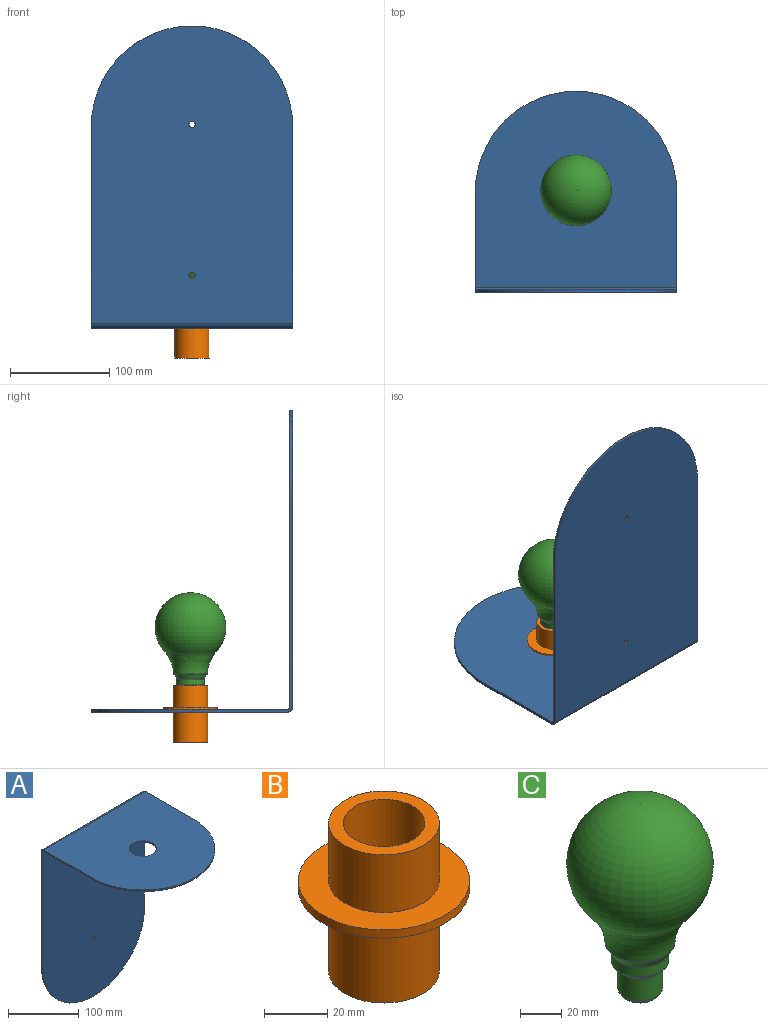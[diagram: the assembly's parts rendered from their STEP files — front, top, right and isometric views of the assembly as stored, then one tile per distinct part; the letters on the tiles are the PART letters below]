
ASSEMBLY  parts=3 mates=1
PART A: 17 faces, bbox 203.2x203.2x304.8 mm
  f0: plane 198.14x2.78mm, normal (1,0,0), area 550.4mm2, adj f4,f5,f6,f13
  f1: plane 198.14x2.78mm, normal (-1,0,0), area 550.4mm2, adj f4,f5,f6,f14
  f2: cylinder r=3.17mm len=6.35mm, axis (0,-1,0), area 55.4mm2, adj f5,f6
  f3: cylinder r=3.17mm len=6.35mm, axis (0,-1,0), area 55.4mm2, adj f5,f6
  f4: cylinder r=101.6mm len=203.2mm, axis (0,-1,0), area 886.7mm2, adj f0,f1,f5,f6
  f5: plane 299.74x203.2mm, normal (0,-1,0), area 56412.5mm2, adj f0,f1,f2,f3,f4,f16
  f6: plane 299.74x203.2mm, normal (0,1,0), area 56412.5mm2, adj f0,f1,f2,f3,f4,f15
  f7: plane 96.54x2.78mm, normal (1,0,0), area 268.2mm2, adj f8,f11,f12,f13
  f8: cylinder r=101.6mm len=203.2mm, axis (0,0,-1), area 886.7mm2, adj f7,f10,f11,f12
  f9: cylinder r=19.05mm len=38.1mm, axis (0,0,-1), area 332.5mm2, adj f11,f12
  f10: plane 96.54x2.78mm, normal (-1,0,0), area 268.2mm2, adj f8,f11,f12,f14
  f11: plane 203.2x198.14mm, normal (0,0,-1), area 34690.6mm2, adj f7,f8,f9,f10,f16
  f12: plane 203.2x198.14mm, normal (0,0,1), area 34690.6mm2, adj f7,f8,f9,f10,f15
  f13: plane 5.06x5.06mm, normal (1,0,0), area 16mm2, adj f0,f7,f15,f16
  f14: plane 5.06x5.06mm, normal (-1,0,0), area 16mm2, adj f1,f10,f15,f16
  f15: cylinder r=5.06mm len=203.2mm, axis (1,0,0), area 1616.4mm2, adj f6,f12,f13,f14
  f16: cylinder r=2.29mm len=203.2mm, axis (1,0,0), area 729.7mm2, adj f5,f11,f13,f14
PART B: 9 faces, bbox 54x54x57.2 mm
  f0: cylinder r=17.46mm len=34.93mm, axis (0,0,-1), area 3483.6mm2, adj f1,f3
  f1: plane 34.93x34.93mm, normal (0,0,-1), area 958mm2, adj f0
  f2: plane 53.98x53.98mm, normal (0,0,1), area 1330.1mm2, adj f4,f5
  f3: plane 53.98x53.98mm, normal (0,0,-1), area 1330.1mm2, adj f0,f4
  f4: cylinder r=26.99mm len=53.98mm, axis (0,0,-1), area 538.4mm2, adj f2,f3
  f5: cylinder r=17.46mm len=34.93mm, axis (0,0,-1), area 2438.5mm2, adj f2,f6
  f6: plane 34.93x34.93mm, normal (0,0,1), area 435.6mm2, adj f5,f7
  f7: cylinder r=12.9mm len=25.79mm, axis (0,0,1), area 1800.8mm2, adj f6,f8
  f8: plane 25.79x25.79mm, normal (0,0,1), area 522.4mm2, adj f7
PART C: 16 faces, bbox 71.4x71.4x112 mm
  f0: torus R=54.7mm, axis (0,0,1), area 2760.8mm2, adj f9,f15
  f1: cone r=17mm half-angle=31deg, axis (0,0,1), area 516.6mm2, adj f9,f10
  f2: cylinder r=14mm len=28mm, axis (0,0,1), area 467mm2, adj f10,f11
  f3: cone r=14mm half-angle=45deg, axis (0,0,1), area 268.2mm2, adj f11,f12
  f4: cylinder r=11mm len=22mm, axis (0,0,1), area 869.9mm2, adj f5,f12
  f5: plane 22x22mm, normal (0,0,-1), area 33.8mm2, adj f4,f13
  f6: cylinder r=9.5mm len=19mm, axis (0,0,1), area 59.7mm2, adj f13,f14
  f7: plane 17x17mm, normal (0,0,-1), area 227mm2, adj f14
  f8: torus R=0.43mm, axis (0,0,1), area 13725.8mm2, adj f15
  f9: torus R=16.01mm, axis (0,0,-1), area 52.3mm2, adj f0,f1
  f10: torus R=15mm, axis (0,0,1), area 47.7mm2, adj f1,f2
  f11: torus R=13mm, axis (0,0,-1), area 68.6mm2, adj f2,f3
  f12: torus R=12mm, axis (0,0,1), area 54.8mm2, adj f3,f4
  f13: torus R=10.5mm, axis (0,0,1), area 97.3mm2, adj f5,f6
  f14: torus R=8.5mm, axis (0,0,1), area 90.2mm2, adj f6,f7
  f15: torus R=25.25mm, axis (0,0,1), area 27.1mm2, adj f0,f8
PLACE A rot(axis=(1,0,0),180deg) t=(140.07,63.08,-200.15)mm
PLACE B rot(axis=(0,0,-1),180deg) t=(241.69,171.44,-132.25)mm
PLACE C t=(241.69,171.44,-37.67)mm
MATE slider B.f7 <-> C.f1  axis (0,0,1) through (241.69,171.44,-75.1)mm
